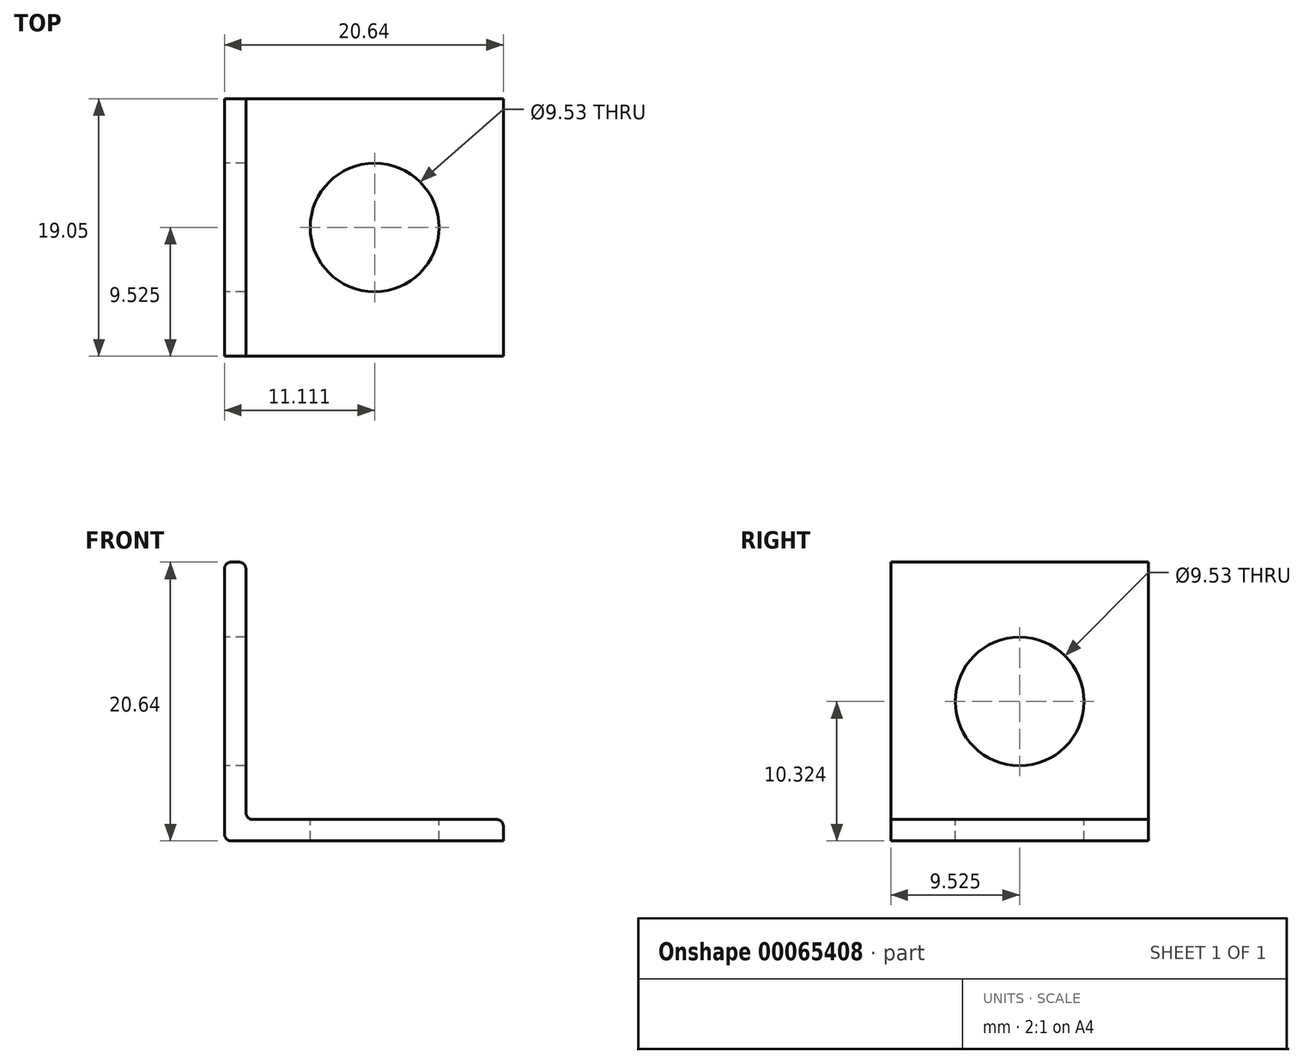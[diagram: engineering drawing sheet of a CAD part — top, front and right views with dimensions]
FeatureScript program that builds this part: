
annotation { "Feature Type Name" : "Feature", "Feature Type Description" : "" }
export const myFeature = defineFeature(function(context is Context, id is Id, definition is map)
    precondition{}
    {
        {
            var Q0;
            Q0=qCreatedBy(makeId("Front.planeOp"),FACE);
            var sketch = newSketch(context, id + "F0", { "sketchPlane" : qUnion([Q0])});
            skLineSegment(sketch, "E0", {"start": v(-27.26, 34.68) * mm, "end": v(-27.26, 14.04) * mm});
            skLineSegment(sketch, "E1", {"start": v(-27.26, 14.04) * mm, "end": v(-6.62, 14.04) * mm});
            skLineSegment(sketch, "E2", {"start": v(-6.62, 14.04) * mm, "end": v(-6.62, 15.63) * mm});
            skLineSegment(sketch, "E3", {"start": v(-6.62, 15.63) * mm, "end": v(-25.67, 15.63) * mm});
            skLineSegment(sketch, "E4", {"start": v(-25.67, 15.63) * mm, "end": v(-25.67, 34.68) * mm});
            skLineSegment(sketch, "E5", {"start": v(-25.67, 34.68) * mm, "end": v(-27.26, 34.68) * mm});
            skSolve(sketch);
        }
        {
            var Q0;
            Q0=makeQuery(id+"F0.imprint","IMPRINT",FACE,{"disambiguationData":[TD([[makeQuery(id+"F0.imprint","IMPRINT",EDGE,{"derivedFrom":sQuery(id+"F0.wireOp",EDGE,"E0")}),1.0]])]});
            extrude(context, id + "F1", {"entities" : qUnion([Q0]), "depth" : 19.05 * mm});
        }
        {
            var Q0;
            Q0=makeQuery(id+"F1.opExtrude","SWEPT_EDGE",EDGE,{"disambiguationData":[OSD([sQuery(id+"F0.wireOp",EDGE,"E0"),sQuery(id+"F0.wireOp",EDGE,"E1")])]});
            var Q1;
            Q1=makeQuery(id+"F1.opExtrude","SWEPT_EDGE",EDGE,{"disambiguationData":[OSD([sQuery(id+"F0.wireOp",EDGE,"E0"),sQuery(id+"F0.wireOp",EDGE,"E5")])]});
            var Q2;
            Q2=makeQuery(id+"F1.opExtrude","SWEPT_EDGE",EDGE,{"disambiguationData":[OSD([sQuery(id+"F0.wireOp",EDGE,"E4"),sQuery(id+"F0.wireOp",EDGE,"E5")])]});
            var Q3;
            Q3=makeQuery(id+"F1.opExtrude","SWEPT_EDGE",EDGE,{"disambiguationData":[OSD([sQuery(id+"F0.wireOp",EDGE,"E2"),sQuery(id+"F0.wireOp",EDGE,"E3")])]});
            var Q4;
            Q4=makeQuery(id+"F1.opExtrude","SWEPT_EDGE",EDGE,{"disambiguationData":[OSD([sQuery(id+"F0.wireOp",EDGE,"E3"),sQuery(id+"F0.wireOp",EDGE,"E4")])]});
            fillet(context, id + "F2", {"entities" : qUnion([Q0, Q1, Q2, Q3, Q4]), "radius" : 0.5 * mm, "tangentPropagation" : true, "allowEdgeOverflow" : false});
        }
        {
            var Q0;
            Q0=makeQuery(id+"F1.opExtrude","SWEPT_FACE",FACE,{"disambiguationData":[OSD([sQuery(id+"F0.wireOp",EDGE,"E0")])]});
            var sketch = newSketch(context, id + "F3", { "sketchPlane" : qUnion([Q0])});
            skLineSegment(sketch, "E6", {"start": v(0, 24.36) * mm, "end": v(19.05, 24.36) * mm});
            skCircle(sketch, "E7", {"center": v(9.53, 24.36) * mm, "radius": 4.76 * mm});
            skSolve(sketch);
        }
        {
            var Q0;
            {var subQ0=sQuery(id+"F3.wireOp",EDGE,"E7");var subQ1=sQuery(id+"F3.wireOp",EDGE,"E6");var subQ2=makeQuery(id+"F3.imprint","INTERSECT",VERTEX,{"disambiguationData":[OD(0.0)],"derivedFrom":[subQ1,subQ0]});Q0=makeQuery(id+"F3.imprint","IMPRINT",FACE,{"disambiguationData":[TD([[makeQuery(id+"F3.imprint","IMPRINT",EDGE,{"disambiguationData":[TD([[subQ2,-1.0]])],"derivedFrom":subQ1}),1.0]])]});}
            var Q1;
            {var subQ0=sQuery(id+"F3.wireOp",EDGE,"E7");var subQ1=sQuery(id+"F3.wireOp",EDGE,"E6");var subQ2=makeQuery(id+"F3.imprint","INTERSECT",VERTEX,{"disambiguationData":[OD(0.0)],"derivedFrom":[subQ1,subQ0]});Q1=makeQuery(id+"F3.imprint","IMPRINT",FACE,{"disambiguationData":[TD([[makeQuery(id+"F3.imprint","IMPRINT",EDGE,{"disambiguationData":[TD([[subQ2,-1.0]])],"derivedFrom":subQ1}),-1.0]])]});}
            extrude(context, id + "F4", {"entities" : qUnion([Q0, Q1]), "operationType" : NewBodyOperationType.REMOVE, "oppositeDirection" : true, "depth" : 25.4 * mm});
        }
        {
            var Q0;
            Q0=makeQuery(id+"F1.opExtrude","SWEPT_FACE",FACE,{"disambiguationData":[OSD([sQuery(id+"F0.wireOp",EDGE,"E3")])]});
            var sketch = newSketch(context, id + "F5", { "sketchPlane" : qUnion([Q0])});
            skLineSegment(sketch, "E8", {"start": v(-25.17, -9.53) * mm, "end": v(-7.13, -9.53) * mm});
            skCircle(sketch, "E9", {"center": v(-16.15, -9.53) * mm, "radius": 4.76 * mm});
            skSolve(sketch);
        }
        {
            var Q0;
            {var subQ0=sQuery(id+"F5.wireOp",EDGE,"E9");var subQ1=sQuery(id+"F5.wireOp",EDGE,"E8");var subQ2=makeQuery(id+"F5.imprint","INTERSECT",VERTEX,{"disambiguationData":[OD(0.0)],"derivedFrom":[subQ1,subQ0]});Q0=makeQuery(id+"F5.imprint","IMPRINT",FACE,{"disambiguationData":[TD([[makeQuery(id+"F5.imprint","IMPRINT",EDGE,{"disambiguationData":[TD([[subQ2,-1.0]])],"derivedFrom":subQ1}),1.0]])]});}
            var Q1;
            {var subQ0=sQuery(id+"F5.wireOp",EDGE,"E9");var subQ1=sQuery(id+"F5.wireOp",EDGE,"E8");var subQ2=makeQuery(id+"F5.imprint","INTERSECT",VERTEX,{"disambiguationData":[OD(0.0)],"derivedFrom":[subQ1,subQ0]});Q1=makeQuery(id+"F5.imprint","IMPRINT",FACE,{"disambiguationData":[TD([[makeQuery(id+"F5.imprint","IMPRINT",EDGE,{"disambiguationData":[TD([[subQ2,-1.0]])],"derivedFrom":subQ1}),-1.0]])]});}
            extrude(context, id + "F6", {"entities" : qUnion([Q0, Q1]), "operationType" : NewBodyOperationType.REMOVE, "oppositeDirection" : true, "depth" : 25.4 * mm});
        }
    });
